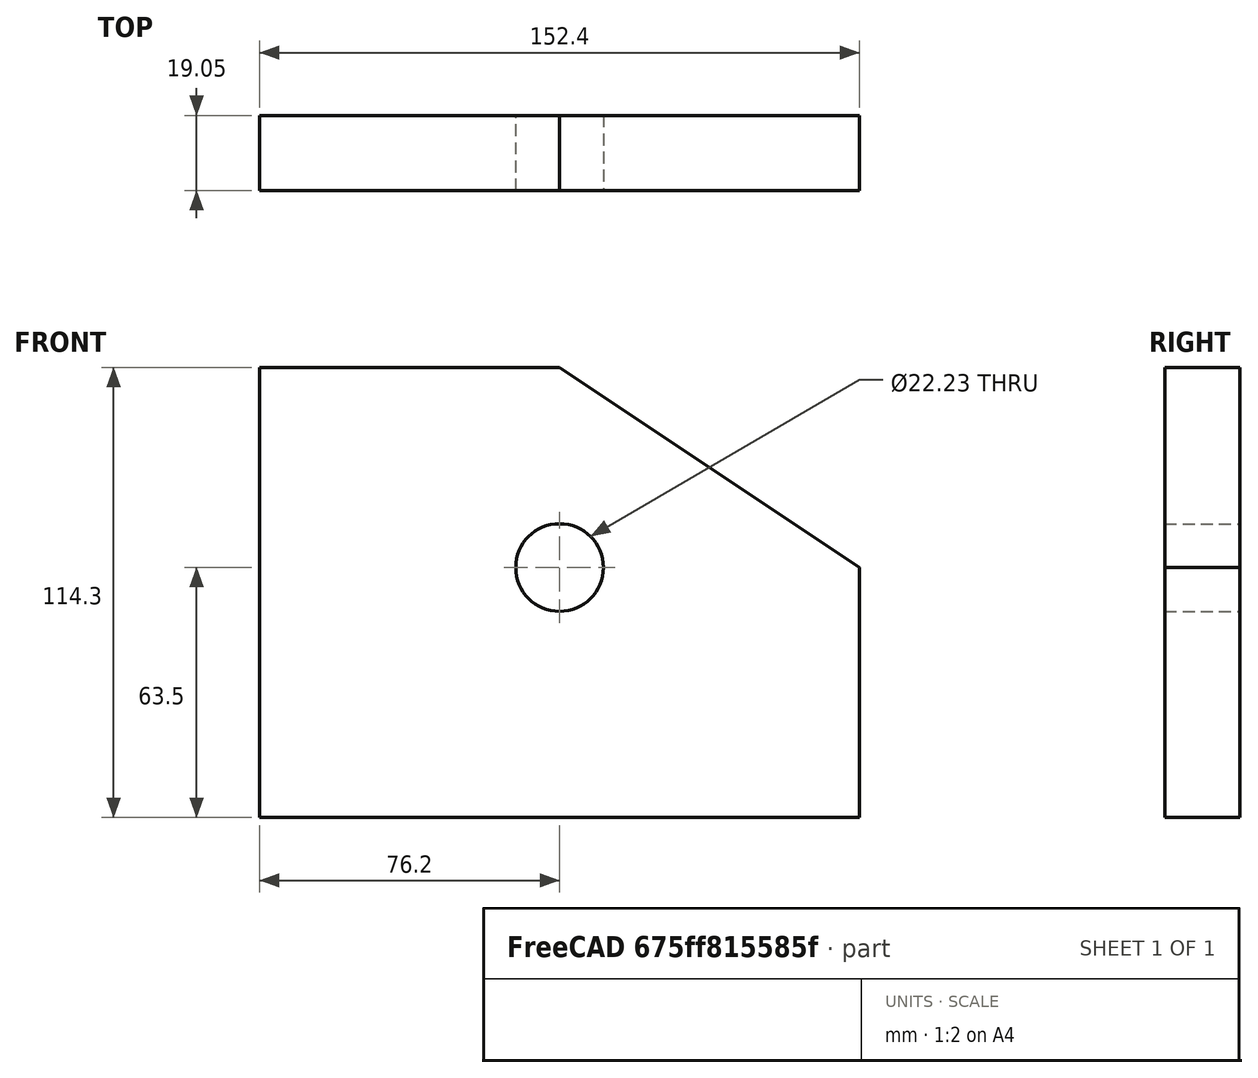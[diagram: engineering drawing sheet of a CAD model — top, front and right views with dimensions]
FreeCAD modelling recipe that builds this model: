
FCSTD DOCUMENT  (FreeCAD 0.20R29603 (Git))
Label: blade_guard
License: All rights reserved
LicenseURL: http://en.wikipedia.org/wiki/All_rights_reserved
objects: TechDraw::DrawViewDimension×5, Sketcher::SketchObject×2, PartDesign::Pad×1, PartDesign::Pocket×1, PartDesign::Body×1, TechDraw::DrawSVGTemplate×1, TechDraw::DrawViewPart×1, TechDraw::DrawPage×1
note: 7 computed .brp shape members not serialized (recipe doc carries the construction recipe); baked Part::Feature solids carry a one-line shape summary decoded from their .brp

FEATURE [Sketcher::SketchObject] Sketch
  FullyConstrained = true
  MapMode = 5
  Placement = pos=(0,0,0) rot=(1,0,0;1.5708rad)
  Support = -> [XZ_Plane]
  sketch-geometry (6):
    g0: LineSegment StartX=-76.2 StartY=-63.5 StartZ=0 EndX=-76.2 EndY=50.8 EndZ=0
    g1: LineSegment StartX=-76.2 StartY=50.8 StartZ=0 EndX=0 EndY=50.8 EndZ=0
    g2: LineSegment StartX=76.2 StartY=0 StartZ=0 EndX=76.2 EndY=-63.5 EndZ=0
    g3: LineSegment StartX=76.2 StartY=-63.5 StartZ=0 EndX=-76.2 EndY=-63.5 EndZ=0
    g4: GeomPoint X=0 Y=0 Z=0
    g5: LineSegment StartX=0 StartY=50.8 StartZ=0 EndX=76.2 EndY=0 EndZ=0
  constraints (16):
    c: Coincident(g0,g1)
    c: Coincident(g2,g3)
    c: Coincident(g3,g0)
    c: Horizontal(g3)
    c: Vertical(g0)
    c: Vertical(g2)
    c: Coincident(g-1,g4)
    c: DistanceY(g0,g0) = 114.3
    c: Horizontal(g1)
    c: DistanceX(g3,g3) = 152.4
    c: Distance(g5,g0) = 76.2
    c: Distance(g5,g2) = 63.5
    c: Coincident(g1,g5)
    c: Coincident(g2,g5)
    c: PointOnObject(g1,g-2)
    c: PointOnObject(g2,g-1)
FEATURE [PartDesign::Pad] Pad
  Direction = (0,-1,-2e-16)
  Length = 19.05
  Length2 = 10
  Placement = pos=(0,0,0) rot=(1,0,0;1.5708rad)
  Profile = -> Sketch
  ReferenceAxis = -> Sketch [N_Axis]
  Type = 0
FEATURE [Sketcher::SketchObject] Sketch001
  ExternalGeometry = -> [Pad]
  FullyConstrained = true
  MapMode = 5
  Placement = pos=(0,0,0) rot=(-1,0,0;1.5708rad)
  Support = -> [Pad]
  sketch-geometry (1):
    g0: Circle CenterX=1.42e-14 CenterY=-7.1e-15 CenterZ=0 NormalX=0 NormalY=0 NormalZ=1 AngleXU=0 Radius=11.1125
  constraints (3):
    c: Diameter(g0) = 22.225
    c: Distance(g0,g-3) = 50.8
    c: Distance(g0,g-4) = 76.2
FEATURE [PartDesign::Pocket] Pocket
  BaseFeature = -> Pad
  Direction = (0,-1,-2e-16)
  Length = 5
  Length2 = 5
  Placement = pos=(0,0,0) rot=(1,0,0;1.5708rad)
  Profile = -> Sketch001
  ReferenceAxis = -> Sketch001 [N_Axis]
  Type = 1
FEATURE [PartDesign::Body] Body
  Group = -> [Sketch,Pad,Sketch001,Pocket]
  Origin = -> Origin
  Tip = -> Pocket
FEATURE [TechDraw::DrawSVGTemplate] Template
  Height = 297
  Orientation = 1
  Width = 420
FEATURE [TechDraw::DrawViewPart] View
  CoarseView = false
  Direction = (0,-1,0)
  Focus = 100
  HardHidden = false
  IsoCount = 0
  IsoHidden = false
  IsoVisible = false
  LockPosition = false
  Perspective = false
  Rotation = 0
  ScaleType = 0
  SeamHidden = false
  SeamVisible = true
  SmoothHidden = false
  SmoothVisible = true
  Source = -> [Body]
  X = 200.253
  XDirection = (1,0,0)
  Y = 164.554
FEATURE [TechDraw::DrawViewDimension] Dimension
  AngleOverride = false
  Arbitrary = false
  ArbitraryTolerances = false
  EqualTolerance = true
  ExtensionAngle = 0
  FormatSpec = %.2w
  FormatSpecOverTolerance = %+.2w
  FormatSpecUnderTolerance = %+.2w
  Inverted = false
  LineAngle = 0
  LockPosition = false
  MeasureType = 1
  OverTolerance = 0
  References2D = -> [View]
  Rotation = 0
  ScaleType = 0
  TheoreticalExact = false
  Type = 2
  UnderTolerance = 0
  X = -96.4401
  Y = 3.2433
FEATURE [TechDraw::DrawViewDimension] Dimension001
  AngleOverride = false
  Arbitrary = false
  ArbitraryTolerances = false
  EqualTolerance = true
  ExtensionAngle = 0
  FormatSpec = %.2w
  FormatSpecOverTolerance = %+.2w
  FormatSpecUnderTolerance = %+.2w
  Inverted = false
  LineAngle = 0
  LockPosition = false
  MeasureType = 1
  OverTolerance = 0
  References2D = -> [View]
  Rotation = 0
  ScaleType = 0
  TheoreticalExact = false
  Type = 1
  UnderTolerance = 0
  X = -7.5712
  Y = -65.9936
FEATURE [TechDraw::DrawViewDimension] Dimension004
  AngleOverride = false
  Arbitrary = false
  ArbitraryTolerances = false
  EqualTolerance = true
  ExtensionAngle = 0
  FormatSpec = %.2w
  FormatSpecOverTolerance = %+.2w
  FormatSpecUnderTolerance = %+.2w
  Inverted = false
  LineAngle = 0
  LockPosition = false
  MeasureType = 1
  OverTolerance = 0
  References2D = -> [View]
  Rotation = 0
  ScaleType = 0
  TheoreticalExact = false
  Type = 1
  UnderTolerance = 0
  X = -32.4955
  Y = 90.8258
FEATURE [TechDraw::DrawViewDimension] Dimension005
  AngleOverride = false
  Arbitrary = false
  ArbitraryTolerances = false
  EqualTolerance = true
  ExtensionAngle = 0
  FormatSpec = %.2w
  FormatSpecOverTolerance = %+.2w
  FormatSpecUnderTolerance = %+.2w
  Inverted = false
  LineAngle = 0
  LockPosition = false
  MeasureType = 1
  OverTolerance = 0
  References2D = -> [View]
  Rotation = 0
  ScaleType = 0
  TheoreticalExact = false
  Type = 2
  UnderTolerance = 0
  X = 154.774
  Y = -37.5189
FEATURE [TechDraw::DrawViewDimension] Dimension006
  AngleOverride = false
  Arbitrary = false
  ArbitraryTolerances = false
  EqualTolerance = true
  ExtensionAngle = 0
  FormatSpec = ⌀%.2w
  FormatSpecOverTolerance = %+.2w
  FormatSpecUnderTolerance = %+.2w
  Inverted = false
  LineAngle = 0
  LockPosition = false
  MeasureType = 1
  OverTolerance = 0
  References2D = -> [View]
  Rotation = 0
  ScaleType = 0
  TheoreticalExact = false
  Type = 5
  UnderTolerance = 0
  X = -21.4678
  Y = -20.8872
FEATURE [TechDraw::DrawPage] Page
  KeepUpdated = true
  NextBalloonIndex = 1
  ProjectionType = 0
  Template = -> Template
  Views = -> [View,Dimension,Dimension001,Dimension004,Dimension005,Dimension006]
